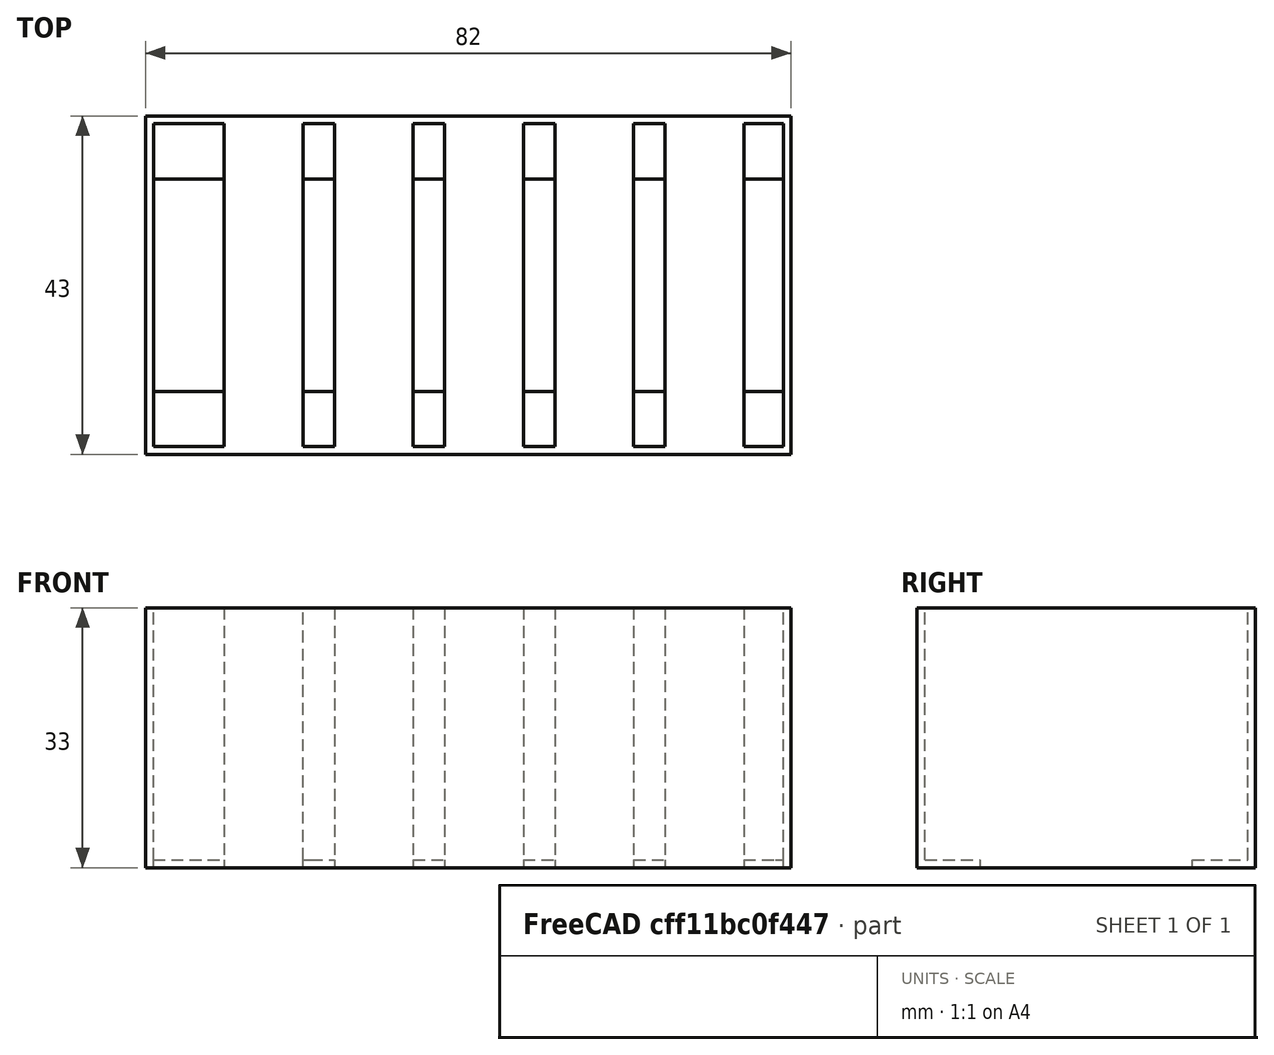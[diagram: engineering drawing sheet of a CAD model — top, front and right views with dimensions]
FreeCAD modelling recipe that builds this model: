
FCSTD DOCUMENT  (FreeCAD 0.18R4 (GitTag))
Label: harbringer
License: All rights reserved
LicenseURL: http://en.wikipedia.org/wiki/All_rights_reserved
objects: Part::Box×18, Part::Cut×5, Part::MultiFuse×5
note: 28 computed .brp shape members not serialized (recipe doc carries the construction recipe); baked Part::Feature solids carry a one-line shape summary decoded from their .brp

FEATURE [Part::Box] Box  label="Cube"
  AttacherType = Attacher::AttachEngine3D
  Height = 33
  Length = 202
  Width = 43
FEATURE [Part::Box] Box001  label="Cube001"
  AttacherType = Attacher::AttachEngine3D
  Height = 33
  Length = 200
  Placement = pos=(1,1,0) rot=(0,0,1;0rad)
  Width = 41
FEATURE [Part::Cut] Cut
  Base = -> Box
  Tool = -> Box001
FEATURE [Part::Box] Box002  label="Cube002"
  AttacherType = Attacher::AttachEngine3D
  Height = 1
  Length = 202
  Width = 8
FEATURE [Part::Box] Box003  label="Cube003"
  AttacherType = Attacher::AttachEngine3D
  Height = 1
  Length = 202
  Placement = pos=(0,35,0) rot=(0,0,1;0rad)
  Width = 8
FEATURE [Part::MultiFuse] Fusion
  Shapes = -> [Cut,Box002,Box003]
FEATURE [Part::Box] Box004  label="Cube004"
  AttacherType = Attacher::AttachEngine3D
  Height = 33
  Length = 10
  Placement = pos=(11,0,0) rot=(0,0,1;0rad)
  Width = 43
FEATURE [Part::Box] Box005  label="Cube005"
  AttacherType = Attacher::AttachEngine3D
  Height = 33
  Length = 10
  Placement = pos=(24,0,0) rot=(0,0,1;0rad)
  Width = 43
FEATURE [Part::Box] Box006  label="Cube006"
  AttacherType = Attacher::AttachEngine3D
  Height = 33
  Length = 10
  Placement = pos=(38,0,0) rot=(0,0,1;0rad)
  Width = 43
FEATURE [Part::Box] Box007  label="Cube007"
  AttacherType = Attacher::AttachEngine3D
  Height = 33
  Length = 10
  Placement = pos=(52,0,0) rot=(0,0,1;0rad)
  Width = 43
FEATURE [Part::Box] Box008  label="Cube008"
  AttacherType = Attacher::AttachEngine3D
  Height = 33
  Length = 10
  Placement = pos=(66,0,0) rot=(0,0,1;0rad)
  Width = 43
FEATURE [Part::Box] Box009  label="Cube009"
  AttacherType = Attacher::AttachEngine3D
  Height = 33
  Length = 10
  Placement = pos=(80,0,0) rot=(0,0,1;0rad)
  Width = 43
FEATURE [Part::Box] Box010  label="Cube010"
  AttacherType = Attacher::AttachEngine3D
  Height = 33
  Length = 121
  Placement = pos=(81,0,0) rot=(0,0,1;0rad)
  Width = 43
FEATURE [Part::MultiFuse] Fusion001
  Shapes = -> [Fusion,Box005,Box006,Box007,Box009,Box004,Box008]
FEATURE [Part::Cut] Cut001
  Base = -> Fusion001
  Tool = -> Box010
FEATURE [Part::Box] Box011  label="Cube011"
  AttacherType = Attacher::AttachEngine3D
  Height = 33
  Length = 1
  Placement = pos=(10,0,0) rot=(0,0,1;0rad)
  Width = 43
FEATURE [Part::Box] Box012  label="Cube012"
  AttacherType = Attacher::AttachEngine3D
  Height = 32
  Length = 1
  Placement = pos=(20,1,1) rot=(0,0,1;0rad)
  Width = 41
FEATURE [Part::MultiFuse] Fusion002
  Shapes = -> [Cut001,Box011]
FEATURE [Part::Cut] Cut002
  Base = -> Fusion002
  Tool = -> Box012
FEATURE [Part::Box] Box013  label="Cube013"
  AttacherType = Attacher::AttachEngine3D
  Height = 1
  Length = 1
  Placement = pos=(20,8,0) rot=(0,0,1;0rad)
  Width = 27
FEATURE [Part::Cut] Cut003
  Base = -> Cut002
  Tool = -> Box013
FEATURE [Part::Box] Box014  label="Cube014"
  AttacherType = Attacher::AttachEngine3D
  Height = 33
  Length = 2
  Placement = pos=(80,0,0) rot=(0,0,1;0rad)
  Width = 43
FEATURE [Part::Box] Box015  label="Cube015"
  AttacherType = Attacher::AttachEngine3D
  Height = 33
  Length = 1
  Placement = pos=(80,1,0) rot=(0,0,1;0rad)
  Width = 41
FEATURE [Part::MultiFuse] Fusion003
  Shapes = -> [Cut003,Box014]
FEATURE [Part::Cut] Cut004
  Base = -> Fusion003
  Tool = -> Box015
FEATURE [Part::Box] Box016  label="Cube016"
  AttacherType = Attacher::AttachEngine3D
  Height = 1
  Length = 1
  Placement = pos=(80,1,0) rot=(0,0,1;0rad)
  Width = 7
FEATURE [Part::Box] Box017  label="Cube017"
  AttacherType = Attacher::AttachEngine3D
  Height = 1
  Length = 1
  Placement = pos=(80,35,0) rot=(0,0,1;0rad)
  Width = 7
FEATURE [Part::MultiFuse] Fusion004
  Shapes = -> [Cut004,Box016,Box017]
